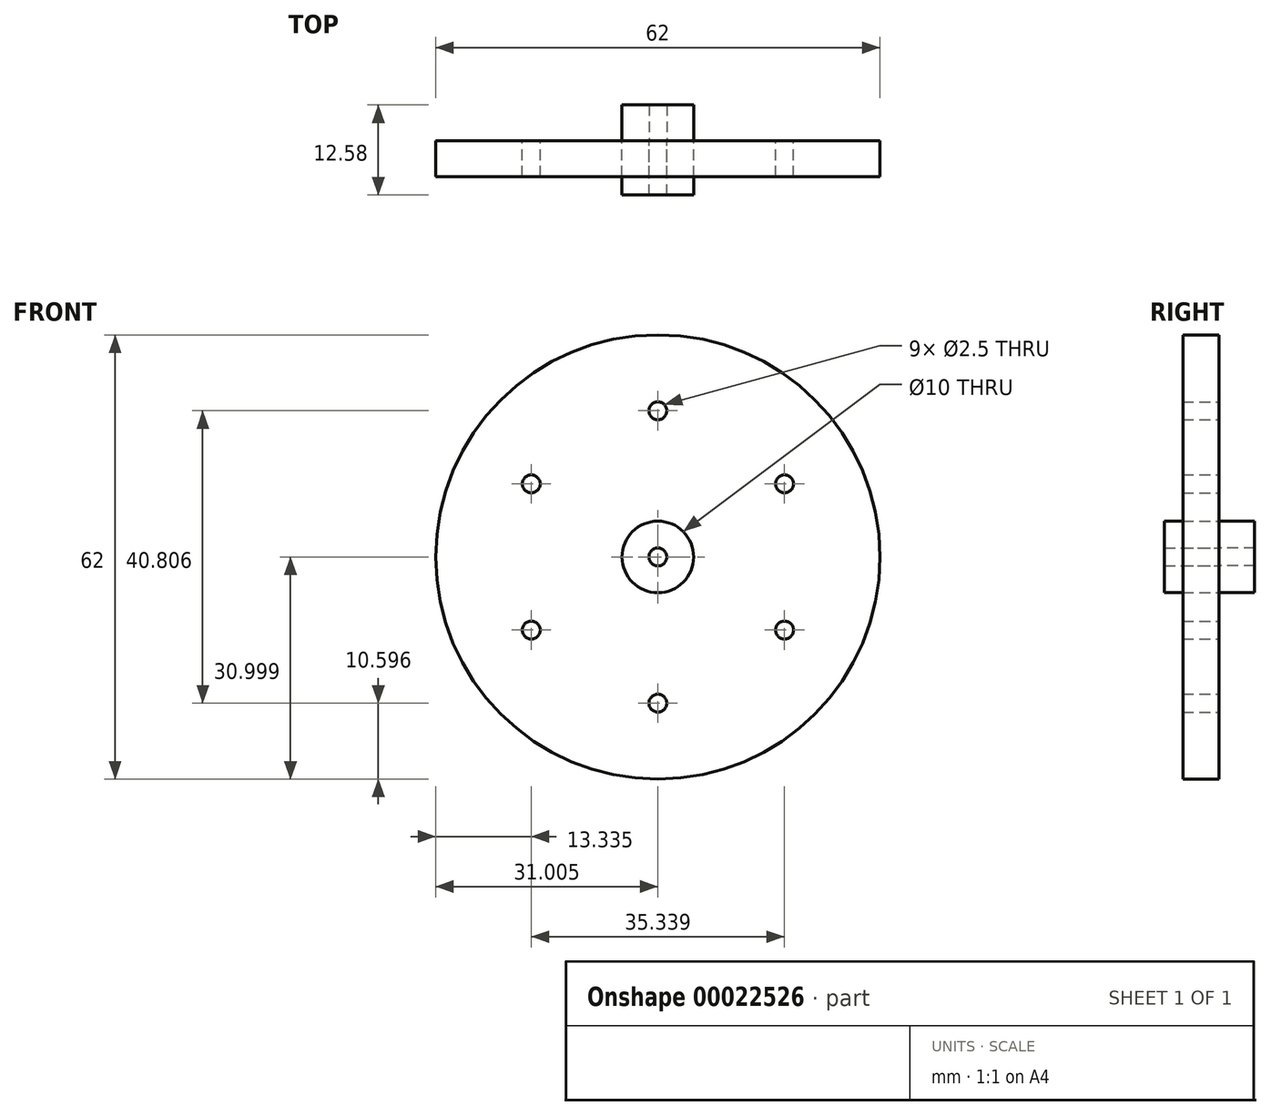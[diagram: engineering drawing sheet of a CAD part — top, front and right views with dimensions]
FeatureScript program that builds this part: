
annotation { "Feature Type Name" : "Feature", "Feature Type Description" : "" }
export const myFeature = defineFeature(function(context is Context, id is Id, definition is map)
    precondition{}
    {
        {
            var Q0;
            Q0=qCreatedBy(makeId("Front.planeOp"),FACE);
            var sketch = newSketch(context, id + "F0", { "sketchPlane" : qUnion([Q0])});
            skCircle(sketch, "E0", {"center": v(-22.27, 6.1) * mm, "radius": 31 * mm});
            skCircle(sketch, "E1", {"center": v(-22.27, 26.51) * mm, "radius": 1.25 * mm});
            skCircle(sketch, "E2.1.0", {"center": v(-4.6, 16.31) * mm, "radius": 1.25 * mm});
            skCircle(sketch, "E2.2.0", {"center": v(-4.6, -4.1) * mm, "radius": 1.25 * mm});
            skCircle(sketch, "E2.3.0", {"center": v(-22.27, -14.3) * mm, "radius": 1.25 * mm});
            skCircle(sketch, "E2.4.0", {"center": v(-39.93, -4.1) * mm, "radius": 1.25 * mm});
            skCircle(sketch, "E2.5.0", {"center": v(-39.93, 16.31) * mm, "radius": 1.25 * mm});
            skLineSegment(sketch, "E2.anchor1", {"start": v(-22.27, 6.1) * mm, "end": v(-22.27, 7.36) * mm, "construction": true});
            skPoint(sketch, "E3.start.orphan", {"position": v(-23.52, 26.51) * mm});
            skCircle(sketch, "E4", {"center": v(-22.27, 6.1) * mm, "radius": 1.25 * mm});
            skCircle(sketch, "E5", {"center": v(-22.27, 6.1) * mm, "radius": 5 * mm});
            skPoint(sketch, "E6.orphan", {"position": v(-22.27, 37.1) * mm});
            skPoint(sketch, "E7.end.orphan", {"position": v(-21.22, 6.8) * mm});
            skLineSegment(sketch, "E8.trimOffspring", {"start": v(-22.27, 25.26) * mm, "end": v(-22.27, 26.51) * mm, "construction": true});
            skSolve(sketch);
        }
        {
            var Q0;
            Q0=makeQuery(id+"F0.imprint","IMPRINT",FACE,{"disambiguationData":[TD([[makeQuery(id+"F0.imprint","IMPRINT",EDGE,{"derivedFrom":sQuery(id+"F0.wireOp",EDGE,"E0")}),1.0]])]});
            extrude(context, id + "F1", {"entities" : qUnion([Q0]), "depth" : 5 * mm});
        }
        {
            var Q0;
            Q0=makeQuery(id+"F0.imprint","IMPRINT",FACE,{"disambiguationData":[TD([[makeQuery(id+"F0.imprint","IMPRINT",EDGE,{"derivedFrom":sQuery(id+"F0.wireOp",EDGE,"E4")}),-1.0]])]});
            extrude(context, id + "F2", {"entities" : qUnion([Q0]), "depth" : 7.58 * mm});
        }
        {
            var Q0;
            Q0=makeQuery(id+"F0.imprint","IMPRINT",FACE,{"disambiguationData":[TD([[makeQuery(id+"F0.imprint","IMPRINT",EDGE,{"derivedFrom":sQuery(id+"F0.wireOp",EDGE,"E4")}),-1.0]])]});
            extrude(context, id + "F3", {"entities" : qUnion([Q0]), "depth" : 5 * mm});
        }
        {
            var Q0;
            Q0=makeQuery(id+"F0.imprint","IMPRINT",FACE,{"disambiguationData":[TD([[makeQuery(id+"F0.imprint","IMPRINT",EDGE,{"derivedFrom":sQuery(id+"F0.wireOp",EDGE,"E4")}),-1.0]])]});
            extrude(context, id + "F4", {"entities" : qUnion([Q0]), "oppositeDirection" : true, "depth" : 5 * mm});
        }
    });
